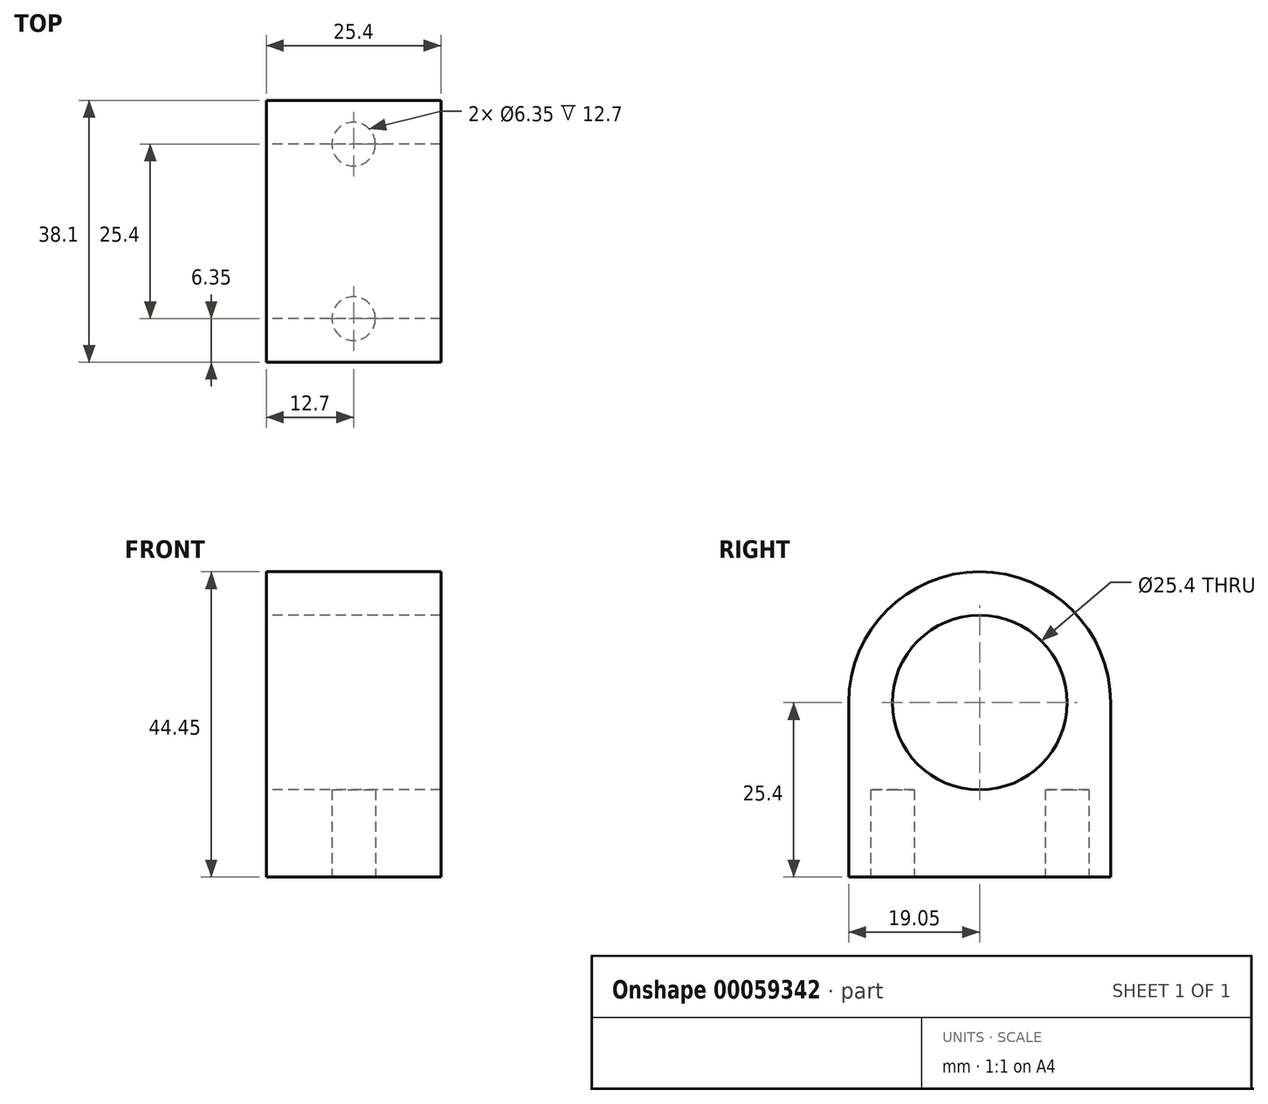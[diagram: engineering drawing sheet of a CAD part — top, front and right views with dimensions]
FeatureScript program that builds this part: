
annotation { "Feature Type Name" : "Feature", "Feature Type Description" : "" }
export const myFeature = defineFeature(function(context is Context, id is Id, definition is map)
    precondition{}
    {
        {
            var Q0;
            Q0=qCreatedBy(makeId("Right.planeOp"),FACE);
            var sketch = newSketch(context, id + "F0", { "sketchPlane" : qUnion([Q0])});
            skLineSegment(sketch, "E0.bottom", {"start": v(-19.05, 0) * mm, "end": v(19.05, 0) * mm});
            skLineSegment(sketch, "E0.top", {"start": v(-19.05, -25.4) * mm, "end": v(19.05, -25.4) * mm});
            skLineSegment(sketch, "E0.left", {"start": v(-19.05, 0) * mm, "end": v(-19.05, -25.4) * mm});
            skLineSegment(sketch, "E0.right", {"start": v(19.05, 0) * mm, "end": v(19.05, -25.4) * mm});
            skCircle(sketch, "E1", {"center": v(0, 0) * mm, "radius": 19.05 * mm});
            skCircle(sketch, "E2", {"center": v(0, 0) * mm, "radius": 12.7 * mm});
            skSolve(sketch);
        }
        {
            var Q0;
            {var subQ1=sQuery(id+"F0.wireOp",EDGE,"E0.bottom");var subQ3=sQuery(id+"F0.wireOp",EDGE,"E2");var subQ4=makeQuery(id+"F0.imprint","INTERSECT",VERTEX,{"disambiguationData":[OD(0.0)],"derivedFrom":[subQ1,subQ3]});Q0=makeQuery(id+"F0.imprint","IMPRINT",FACE,{"disambiguationData":[TD([[makeQuery(id+"F0.imprint","IMPRINT",EDGE,{"disambiguationData":[TD([[subQ4,1.0]])],"derivedFrom":subQ3}),-1.0]])]});}
            var Q1;
            {var subQ1=sQuery(id+"F0.wireOp",EDGE,"E0.bottom");var subQ3=sQuery(id+"F0.wireOp",EDGE,"E2");var subQ4=makeQuery(id+"F0.imprint","INTERSECT",VERTEX,{"disambiguationData":[OD(0.0)],"derivedFrom":[subQ1,subQ3]});Q1=makeQuery(id+"F0.imprint","IMPRINT",FACE,{"disambiguationData":[TD([[makeQuery(id+"F0.imprint","IMPRINT",EDGE,{"disambiguationData":[TD([[subQ4,-1.0]])],"derivedFrom":subQ3}),-1.0]])]});}
            var Q2;
            Q2=makeQuery(id+"F0.imprint","IMPRINT",FACE,{"disambiguationData":[TD([[makeQuery(id+"F0.imprint","IMPRINT",EDGE,{"derivedFrom":sQuery(id+"F0.wireOp",EDGE,"E0.top")}),1.0]])]});
            extrude(context, id + "F1", {"entities" : qUnion([Q0, Q1, Q2]), "depth" : 25.4 * mm});
        }
        {
            var Q0;
            Q0=makeQuery(id+"F1.opExtrude","SWEPT_FACE",FACE,{"disambiguationData":[OSD([sQuery(id+"F0.wireOp",EDGE,"E0.top")])]});
            var sketch = newSketch(context, id + "F2", { "sketchPlane" : qUnion([Q0])});
            skCircle(sketch, "E3", {"center": v(12.7, 12.7) * mm, "radius": 3.18 * mm});
            skCircle(sketch, "E4", {"center": v(12.7, -12.7) * mm, "radius": 3.18 * mm});
            skSolve(sketch);
        }
        {
            var Q0;
            Q0=makeQuery(id+"F2.imprint","IMPRINT",FACE,{"disambiguationData":[TD([[makeQuery(id+"F2.imprint","IMPRINT",EDGE,{"derivedFrom":sQuery(id+"F2.wireOp",EDGE,"E3")}),1.0]])]});
            var Q1;
            Q1=makeQuery(id+"F2.imprint","IMPRINT",FACE,{"disambiguationData":[TD([[makeQuery(id+"F2.imprint","IMPRINT",EDGE,{"derivedFrom":sQuery(id+"F2.wireOp",EDGE,"E4")}),1.0]])]});
            extrude(context, id + "F3", {"entities" : qUnion([Q0, Q1]), "operationType" : NewBodyOperationType.REMOVE, "oppositeDirection" : true, "depth" : 12.7 * mm});
        }
    });
